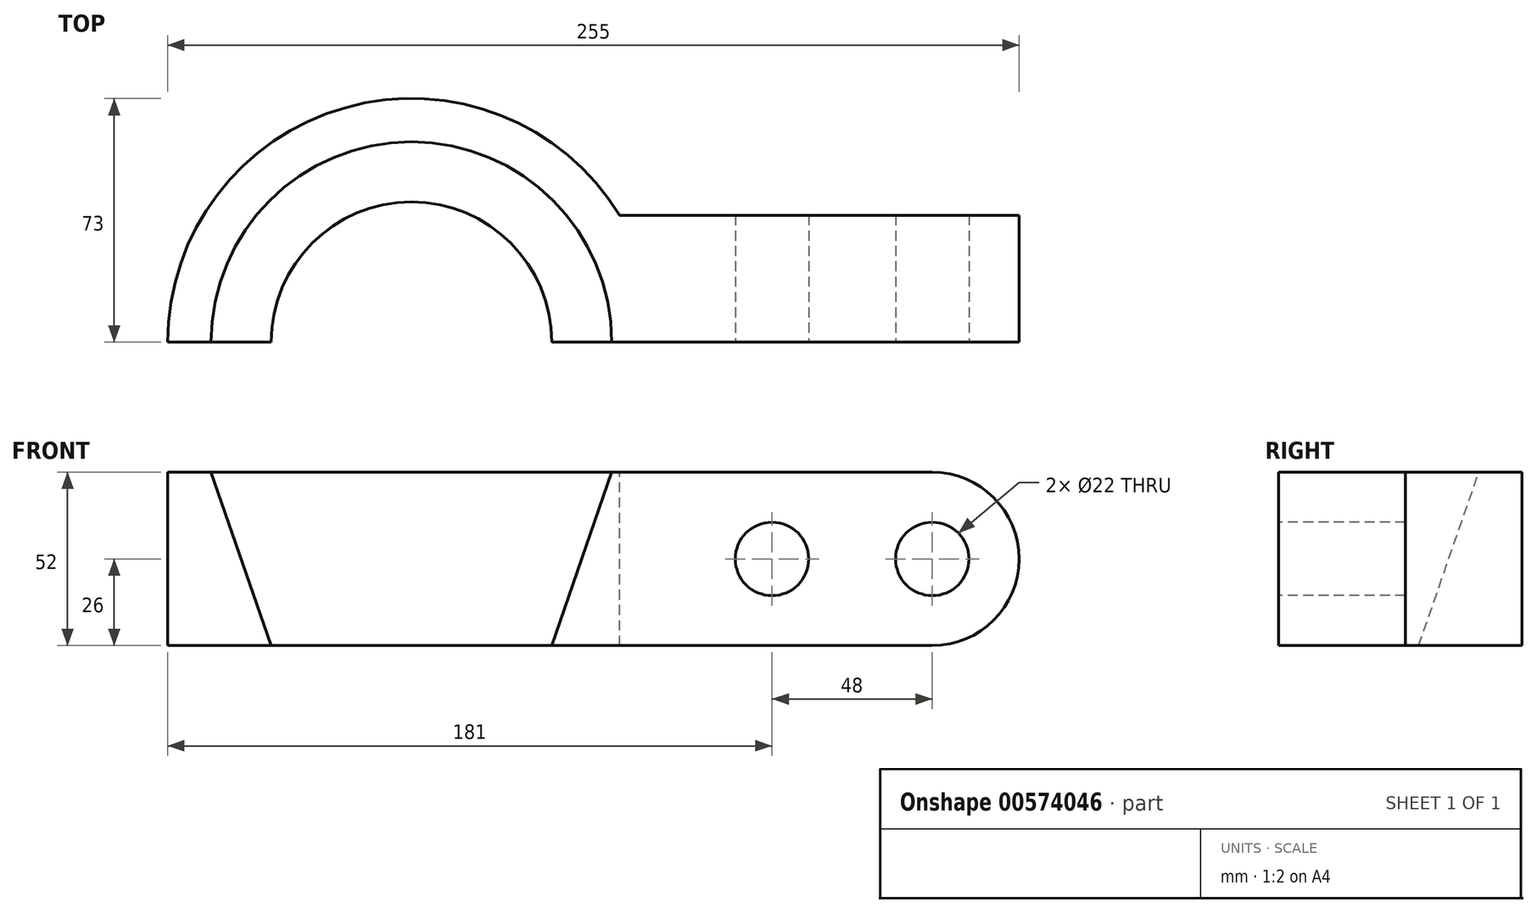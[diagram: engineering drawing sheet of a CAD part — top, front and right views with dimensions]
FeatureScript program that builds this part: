
annotation { "Feature Type Name" : "Feature", "Feature Type Description" : "" }
export const myFeature = defineFeature(function(context is Context, id is Id, definition is map)
    precondition{}
    {
        {
            var Q0;
            Q0=qCreatedBy(makeId("Front.planeOp"),FACE);
            var sketch = newSketch(context, id + "F0", { "sketchPlane" : qUnion([Q0])});
            skLineSegment(sketch, "E0", {"start": v(-42, 0) * mm, "end": v(-73, 0) * mm});
            skLineSegment(sketch, "E1", {"start": v(-73, 0) * mm, "end": v(-73, 52) * mm});
            skLineSegment(sketch, "E2", {"start": v(-73, 52) * mm, "end": v(-60, 52) * mm});
            skLineSegment(sketch, "E3", {"start": v(-60, 52) * mm, "end": v(-42, 0) * mm});
            skSolve(sketch);
        }
        {
            var Q0;
            Q0=qCreatedBy(makeId("Front.planeOp"),FACE);
            var sketch = newSketch(context, id + "F1", { "sketchPlane" : qUnion([Q0])});
            skLineSegment(sketch, "E4", {"start": v(0, 0) * mm, "end": v(0, 57.07) * mm, "construction": true});
            skSolve(sketch);
        }
        {
            var Q0;
            Q0=makeQuery(id+"F0.imprint","IMPRINT",FACE,{"disambiguationData":[TD([[makeQuery(id+"F0.imprint","IMPRINT",EDGE,{"derivedFrom":sQuery(id+"F0.wireOp",EDGE,"E0")}),-1.0]])]});
            var Q1;
            Q1=sQuery(id+"F1.wireOp",EDGE,"E4");
            revolve(context, id + "F2", {"entities" : qUnion([Q0]), "axis" : qUnion([Q1]), "revolveType" : RevolveType.ONE_DIRECTION, "oppositeDirection" : true, "angle" : 180 * degree});
        }
        {
            var Q0;
            Q0=qCreatedBy(makeId("Front.planeOp"),FACE);
            var sketch = newSketch(context, id + "F3", { "sketchPlane" : qUnion([Q0])});
            skLineSegment(sketch, "E5", {"start": v(60, 52) * mm, "end": v(156, 52) * mm});
            skLineSegment(sketch, "E6", {"start": v(42, 0) * mm, "end": v(156, 0) * mm});
            skArc(sketch, "E7", {"start": v(156, 52) * mm, "mid": v(182, 26) * mm, "end": v(156, 0) * mm});
            skLineSegment(sketch, "E8", {"start": v(60, 52) * mm, "end": v(42, 0) * mm});
            skCircle(sketch, "E9", {"center": v(156, 26) * mm, "radius": 11 * mm});
            skCircle(sketch, "E10", {"center": v(108, 26) * mm, "radius": 11 * mm});
            skSolve(sketch);
        }
        {
            var Q0;
            Q0 = qSketchRegion(id + "F3", true);
            extrude(context, id + "F4", {"entities" : qUnion([Q0]), "operationType" : NewBodyOperationType.ADD, "oppositeDirection" : true, "depth" : 38 * mm, "offsetDistance" : 25 * mm});
        }
    });
